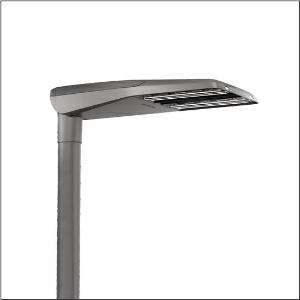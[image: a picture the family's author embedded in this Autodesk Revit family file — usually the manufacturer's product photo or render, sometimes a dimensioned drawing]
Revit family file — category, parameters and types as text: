
# Revit family: streetlight_sl_11_iq_midi___st1_2a_5xc3a41f08me_055e
name_source: partatom
category: Lighting Fixtures
units: mm (PartAtom-declared; Revit-internal decimal feet)

## family parameters
Cut with Voids When Loaded = No
Host = Face
Light Source = No
Part Type = Normal
Room Calculation Point = No
Round Connector Dimension = Use Diameter
Shared = No

## types (1)
- --- (1 x LED, 18900 lm, 124.7 W, 4000K)
    Apparent Load = 125 VA
    CIE Flux Codes = 32 70 96 100 100
    Color Rendering = 70
    Color Temperature = 4000K
    Default Elevation = 1800 mm
    Description = Streetlight SL 11 iQ midi, mast luminaire, primary light control with 3 zone facetted reflector, of plastic, silver coated, highly specular, primary optical cover: cover, of PMMA, transparent, light distribution: ST1.2a, light emission: direct distribution, primary light characteristic: asymmetric, installation type: post-top, side-entry, LED, High Power LED, rated luminous flux: 18.900lm, luminous efficacy: 152lm/W, light colour: 740, colour temperature: 4000K, control: Street-Remote, optimised constant luminous flux control (CLO 2.0), Desk-Remote (wireless, voltage-free reading and setting of iQ features in the workshop via application-optimized NFC function/RFID function), Light-Fading, Smart-Wire, Night-Set, Lumen-Switch, Temp-Guard, Auto-Match, with cable H07RN-F 5x 1.5mm², mains connection: 230..240V, AC, 50/60Hz, connection cable pre-assembled, cable length: 12,5m, start of lifetime: 125W, end of service life: 132W, reduction: 57W, luminaire housing, of diecast aluminium, powder-coated, Siteco® metallic grey (DB 702S), please order mast flange separately, inclination adjustable without tools: 0°, 5°, 10°, 15° (post-top) | 0°, -5°, -10°, -15° (side-entry), sealing non-destructively replaceable, multi-level sealing system, length: 780mm, width: 376mm, height: 118mm, mast flange for spigot size: 42mm (side-entry): 5XC10008XM4, 60/48mm (side-entry/post-top): 5XC10108XM2, 76/60mm (side-entry/post-top): 5XC10108XM1, equipment: Power, protection rating (complete): IP66, insulation class (complete): insulation class II (safety insulation), certification: CE, ENEC, VDE, impact resistance: IK09, permissible operating ambient temperature for outdoor applications: -25..+50°C, standard-compliant lighting for roads and squares, Environmental Product Declaration (EPD) tested and certified by an independent institute, packaging unit: 1 piece

Light Distribution: ST1.2a
    Height = 118 mm
    Lamp = 1 x LED
    Lamp Light Flux = 18900 lm
    Lamp Power = 124.7 W
    Lamp count = 1
    Length = 780 mm
    Luminous efficacy = 152 lm/W
    Manufacturer = Siteco
    ModVariant = No
    Model = 5XC3A41F08ME
    Number of Poles = 1
    OnlyDefault = Yes
    Power Factor = 1
    Product Name = Streetlight SL 11 iQ midi | ST1.2a
    Product group = mast luminaire | pylon top
    ProductGroupID = 6100
    Protection Class = Protection class II
    Protection Degree = IP 66
    RLX_Detail_Level = 1
    RLX_Emergency_Light_Flux = 0 lm
    RLX_Emergency_Type = 0
    RLX_Emergency_Type_DB = No
    RlxData = <blob elided: 70825 chars, md5=78be9a7e>
    Socket = socket
    Standby Power = 0 W
    System Light Flux = 18900 lm
    System Power = 125 W
    Type Comments = factory setting: luminous flux: 100 % | dim-lin: 254 | 557 mA
    Type Image = l_1005960.jpg
    URL = http://relux.com
    VarID = @adj_131775
    Voltage = 0 V
    Weight = 0.00 kg
    Width = 376 mm

## geometry (parser evidence)
native form markers: Blend x4, Sweep x11
no freeform markers — native parametric forms only
